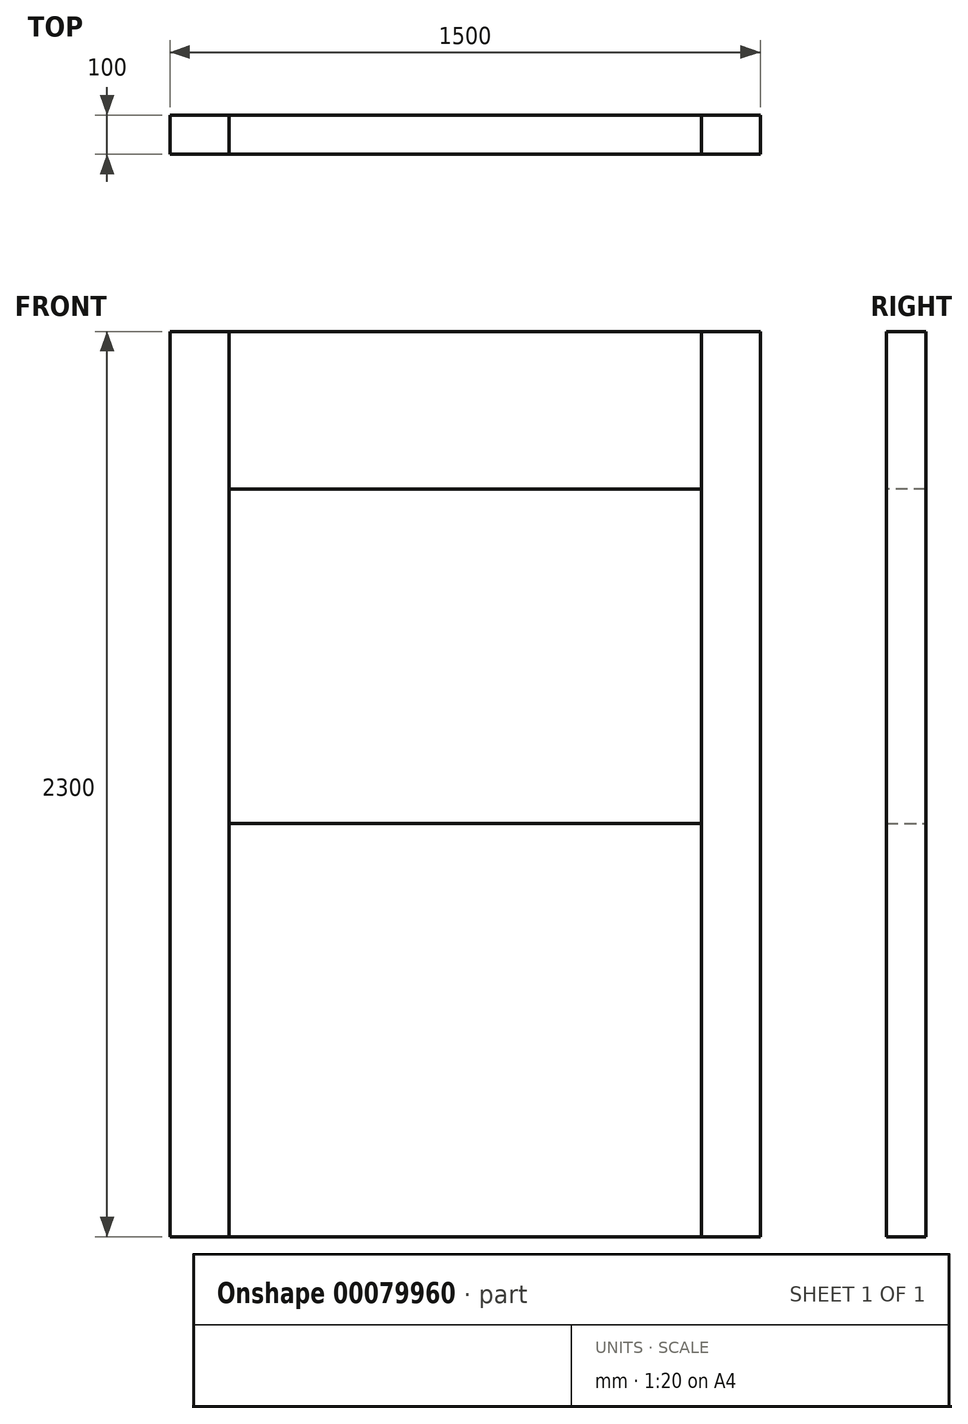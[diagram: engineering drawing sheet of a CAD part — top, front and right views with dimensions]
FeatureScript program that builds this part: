
annotation { "Feature Type Name" : "Feature", "Feature Type Description" : "" }
export const myFeature = defineFeature(function(context is Context, id is Id, definition is map)
    precondition{}
    {
        {
            var Q0;
            Q0=qCreatedBy(makeId("Front.planeOp"),FACE);
            var sketch = newSketch(context, id + "F0", { "sketchPlane" : qUnion([Q0])});
            skLineSegment(sketch, "E0.bottom", {"start": v(600, 525) * mm, "end": v(-600, 525) * mm});
            skLineSegment(sketch, "E0.top", {"start": v(600, -525) * mm, "end": v(-600, -525) * mm});
            skLineSegment(sketch, "E0.left", {"start": v(600, 525) * mm, "end": v(600, -525) * mm});
            skLineSegment(sketch, "E0.right", {"start": v(-600, 525) * mm, "end": v(-600, -525) * mm});
            skPoint(sketch, "E0.middle", {"position": v(0, 0) * mm});
            skSolve(sketch);
        }
        {
            var Q0;
            Q0 = qSketchRegion(id + "F0", true);
            extrude(context, id + "F1", {"entities" : qUnion([Q0]), "depth" : 100 * mm});
        }
        {
            var Q0;
            Q0=makeQuery(id+"F1.opExtrude","SWEPT_FACE",FACE,{"disambiguationData":[OSD([sQuery(id+"F0.wireOp",EDGE,"E0.top")])]});
            var sketch = newSketch(context, id + "F2", { "sketchPlane" : qUnion([Q0])});
            skLineSegment(sketch, "E1.bottom", {"start": v(600, 100) * mm, "end": v(750, 100) * mm});
            skLineSegment(sketch, "E1.top", {"start": v(600, 0) * mm, "end": v(750, 0) * mm});
            skLineSegment(sketch, "E1.left", {"start": v(600, 100) * mm, "end": v(600, 0) * mm});
            skLineSegment(sketch, "E1.right", {"start": v(750, 100) * mm, "end": v(750, 0) * mm});
            skLineSegment(sketch, "E2.bottom", {"start": v(-600, 100) * mm, "end": v(-750, 100) * mm});
            skLineSegment(sketch, "E2.top", {"start": v(-600, 0) * mm, "end": v(-750, 0) * mm});
            skLineSegment(sketch, "E2.left", {"start": v(-600, 100) * mm, "end": v(-600, 0) * mm});
            skLineSegment(sketch, "E2.right", {"start": v(-750, 100) * mm, "end": v(-750, 0) * mm});
            skSolve(sketch);
        }
        {
            var Q0;
            Q0 = qSketchRegion(id + "F2", true);
            extrude(context, id + "F3", {"entities" : qUnion([Q0]), "oppositeDirection" : true, "depth" : 2300 * mm});
        }
        {
            var Q0;
            Q0=makeQuery(id+"F3.opExtrude","SWEPT_FACE",FACE,{"disambiguationData":[OSD([sQuery(id+"F2.wireOp",EDGE,"E2.bottom")])]});
            var sketch = newSketch(context, id + "F4", { "sketchPlane" : qUnion([Q0])});
            skLineSegment(sketch, "E3.bottom", {"start": v(-600, 1775) * mm, "end": v(600, 1775) * mm});
            skLineSegment(sketch, "E3.top", {"start": v(-600, 1375) * mm, "end": v(600, 1375) * mm});
            skLineSegment(sketch, "E3.left", {"start": v(-600, 1775) * mm, "end": v(-600, 1375) * mm});
            skLineSegment(sketch, "E3.right", {"start": v(600, 1775) * mm, "end": v(600, 1375) * mm});
            skSolve(sketch);
        }
        {
            var Q0;
            Q0 = qSketchRegion(id + "F4", true);
            var Q1;
            Q1=makeQuery(id+"F3.opExtrude","SWEPT_FACE",FACE,{"disambiguationData":[OSD([sQuery(id+"F2.wireOp",EDGE,"E1.top")])]});
            extrude(context, id + "F5", {"entities" : qUnion([Q0]), "endBound" : BoundingType.UP_TO_SURFACE, "oppositeDirection" : true, "endBoundEntityFace" : qUnion([Q1]), "depth" : 25 * mm});
        }
    });
